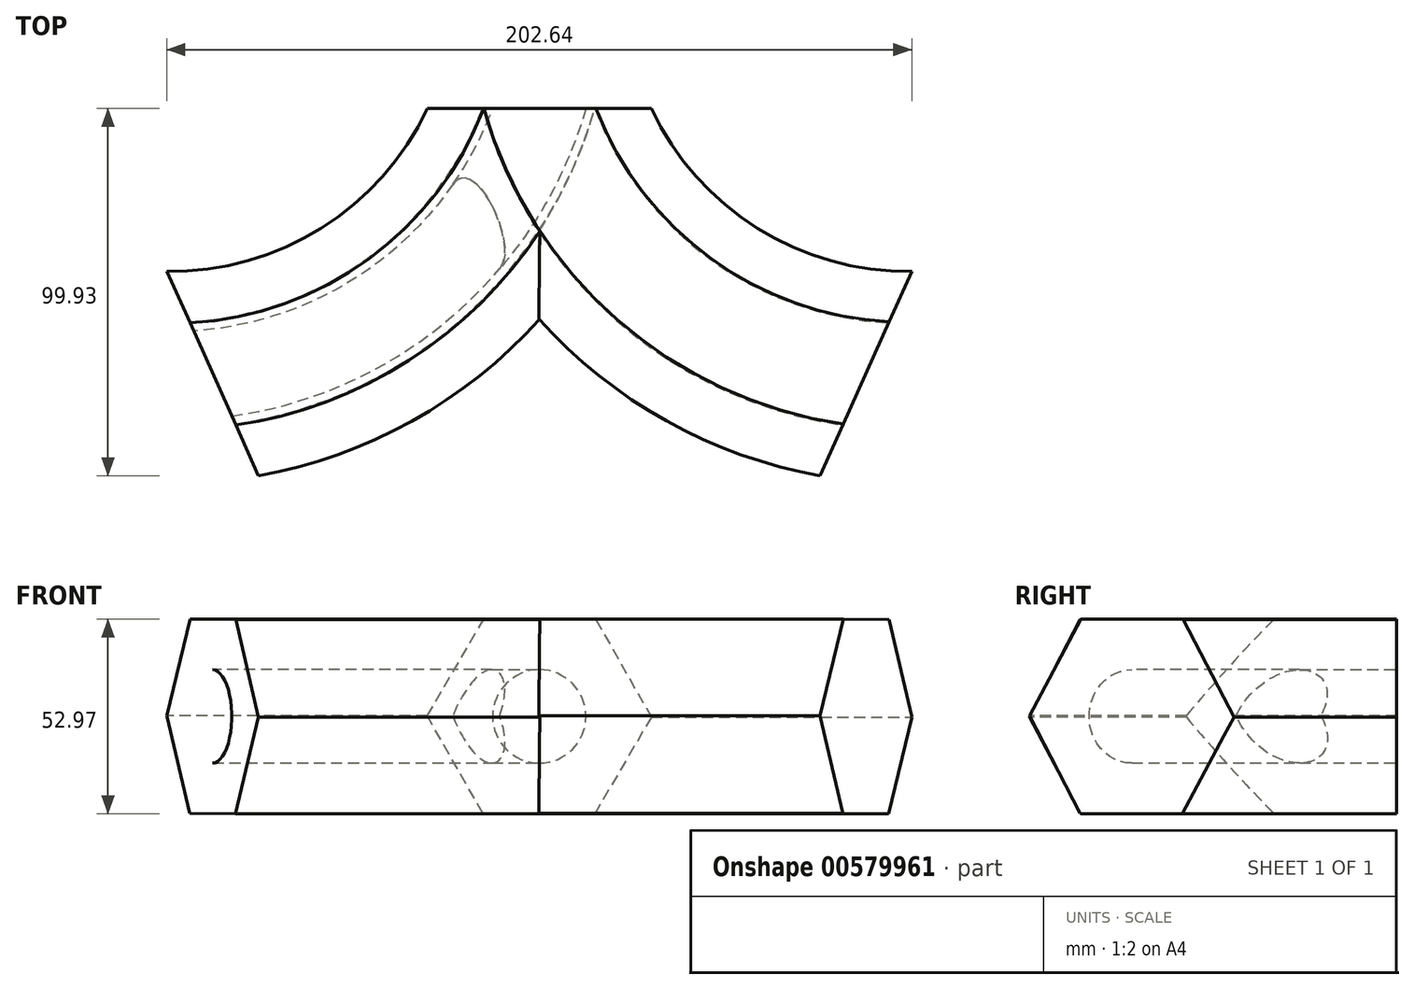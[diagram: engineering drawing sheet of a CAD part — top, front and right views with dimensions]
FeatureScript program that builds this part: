
annotation { "Feature Type Name" : "Feature", "Feature Type Description" : "" }
export const myFeature = defineFeature(function(context is Context, id is Id, definition is map)
    precondition{}
    {
        {
            var Q0;
            Q0=qCreatedBy(makeId("Front.planeOp"),FACE);
            var sketch = newSketch(context, id + "F0", { "sketchPlane" : qUnion([Q0])});
            skCircle(sketch, "E0.cCircle", {"center": v(0, 26.89) * mm, "radius": 26.4 * mm, "construction": true});
            skLineSegment(sketch, "E0.0", {"start": v(-15.4, 0.58) * mm, "end": v(-30.48, 27.07) * mm});
            skLineSegment(sketch, "E0.1", {"start": v(-30.48, 27.07) * mm, "end": v(-15.08, 53.37) * mm});
            skLineSegment(sketch, "E0.2", {"start": v(-15.08, 53.37) * mm, "end": v(15.4, 53.2) * mm});
            skLineSegment(sketch, "E0.3", {"start": v(15.4, 53.2) * mm, "end": v(30.48, 26.7) * mm});
            skLineSegment(sketch, "E0.4", {"start": v(30.48, 26.7) * mm, "end": v(15.08, 0.4) * mm});
            skLineSegment(sketch, "E0.5", {"start": v(15.08, 0.4) * mm, "end": v(-15.4, 0.58) * mm});
            skPoint(sketch, "E0.0.midPoint", {"position": v(-22.94, 13.82) * mm});
            skCircle(sketch, "E1", {"center": v(0, 26.89) * mm, "radius": 12.7 * mm});
            skSolve(sketch);
        }
        {
            var Q0;
            Q0=qCreatedBy(makeId("Top.planeOp"),FACE);
            var sketch = newSketch(context, id + "F1", { "sketchPlane" : qUnion([Q0])});
            skArc(sketch, "E2", {"start": v(-88.86, -72.11) * mm, "mid": v(-33.77, -49.2) * mm, "end": v(0, 0) * mm});
            skArc(sketch, "E3.MirrorCS", {"start": v(88.86, -72.11) * mm, "mid": v(33.77, -49.2) * mm, "end": v(0, 0) * mm});
            skSolve(sketch);
        }
        {
            var Q0;
            Q0=makeQuery(id+"F0.imprint","IMPRINT",FACE,{"disambiguationData":[TD([[makeQuery(id+"F0.imprint","IMPRINT",EDGE,{"derivedFrom":sQuery(id+"F0.wireOp",EDGE,"E0.0")}),-1.0]])]});
            var Q1;
            Q1=sQuery(id+"F1.wireOp",EDGE,"E2");
            sweep(context, id + "F2", {"profiles" : qUnion([Q0]), "path" : qUnion([Q1])});
        }
        {
            var Q0;
            Q0 = qSketchRegion(id + "F0", true);
            var Q1;
            Q1=makeQuery(id+"F0.imprint","IMPRINT",FACE,{"disambiguationData":[TD([[makeQuery(id+"F0.imprint","IMPRINT",EDGE,{"derivedFrom":sQuery(id+"F0.wireOp",EDGE,"E1")}),1.0]])]});
            var Q2;
            Q2=sQuery(id+"F1.wireOp",EDGE,"E3.MirrorCS");
            sweep(context, id + "F3", {"operationType" : NewBodyOperationType.ADD, "profiles" : qUnion([Q0, Q1]), "path" : qUnion([Q2])});
        }
        {
            var Q0;
            Q0=makeQuery(id+"F0.imprint","IMPRINT",FACE,{"disambiguationData":[TD([[makeQuery(id+"F0.imprint","IMPRINT",EDGE,{"derivedFrom":sQuery(id+"F0.wireOp",EDGE,"E1")}),1.0]])]});
            var Q1;
            Q1=sQuery(id+"F1.wireOp",EDGE,"E2");
            sweep(context, id + "F4", {"operationType" : NewBodyOperationType.REMOVE, "profiles" : qUnion([Q0]), "path" : qUnion([Q1])});
        }
    });
